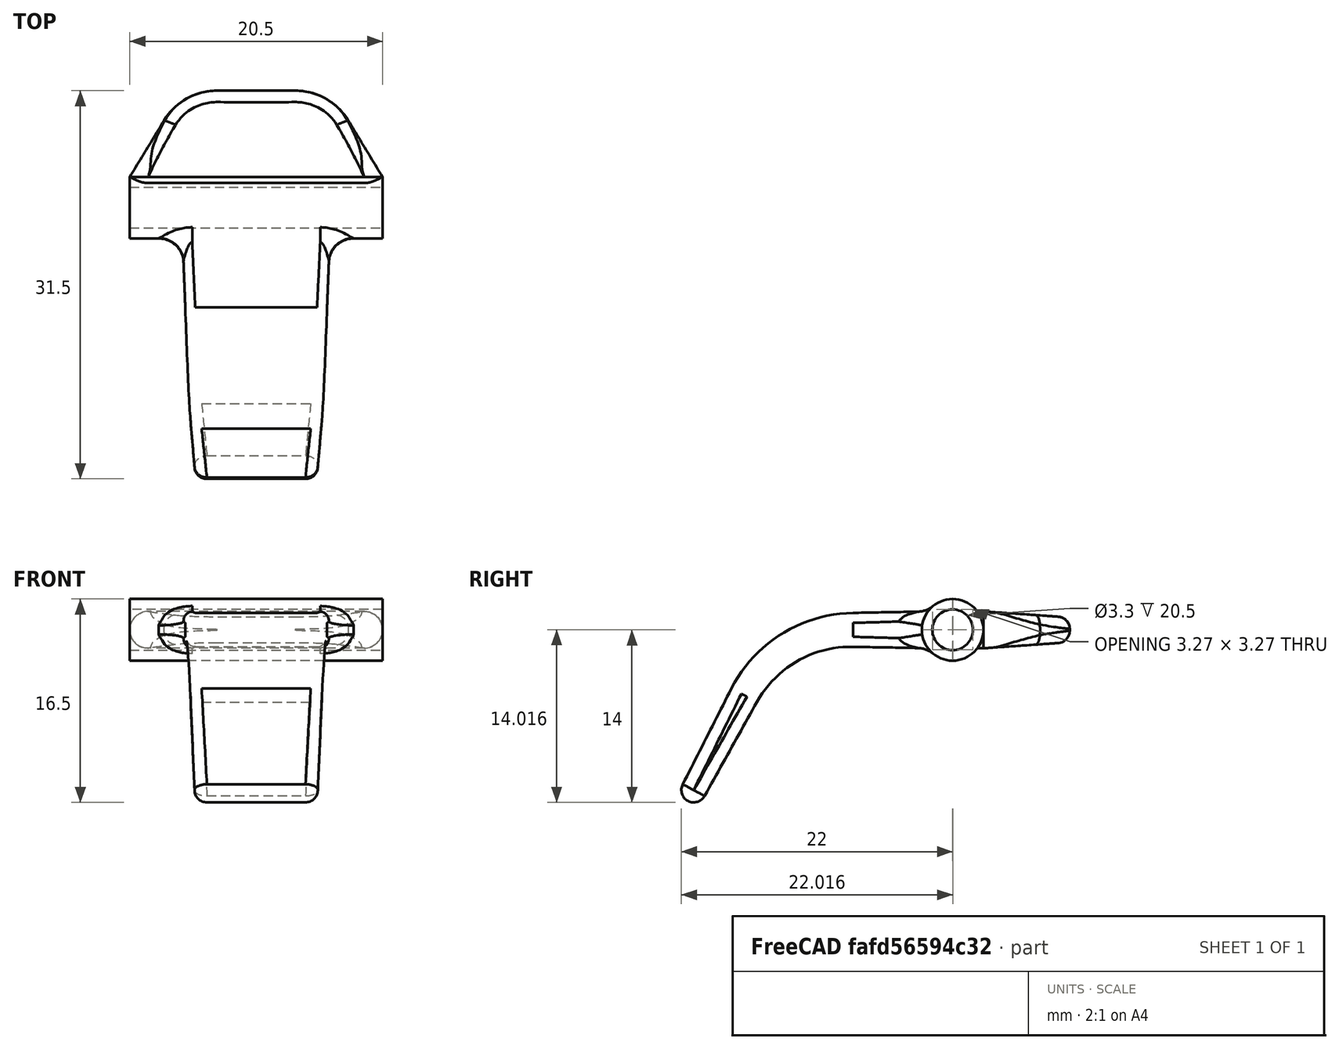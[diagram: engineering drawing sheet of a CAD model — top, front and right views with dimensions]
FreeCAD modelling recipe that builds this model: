
FCSTD DOCUMENT  (FreeCAD 0.20R28671 (Git))
Label: lengueta
License: All rights reserved
LicenseURL: http://en.wikipedia.org/wiki/All_rights_reserved
objects: TechDraw::DrawViewDimension×26, TechDraw::DrawViewAnnotation×10, Sketcher::SketchObject×8, PartDesign::Plane×5, TechDraw::DrawViewPart×5, TechDraw::DrawLeaderLine×4, PartDesign::Fillet×3, PartDesign::Pad×2, TechDraw::DrawProjGroupItem×2, TechDraw::DrawViewSection×2, PartDesign::AdditiveLoft×1, PartDesign::Pocket×1, PartDesign::AdditivePipe×1, PartDesign::Revolution×1, PartDesign::Body×1, TechDraw::DrawSVGTemplate×1, TechDraw::DrawProjGroup×1, TechDraw::DrawPage×1
note: 32 computed .brp shape members not serialized (recipe doc carries the construction recipe); baked Part::Feature solids carry a one-line shape summary decoded from their .brp

FEATURE [Sketcher::SketchObject] Sketch
  FullyConstrained = true
  MapMode = 5
  Placement = pos=(0,0,0) rot=(0.57735,0.57735,0.57735;2.0944rad)
  Support = -> [YZ_Plane]
  sketch-geometry (2):
    g0: Circle CenterX=0 CenterY=0 CenterZ=0 NormalX=0 NormalY=0 NormalZ=1 AngleXU=0 Radius=1.7
    g1: Circle CenterX=0 CenterY=0 CenterZ=0 NormalX=0 NormalY=0 NormalZ=1 AngleXU=0 Radius=2.5
  constraints (4):
    c: Coincident(g0,g-1)
    c: Diameter(g0) = 3.4
    c: Coincident(g1,g0)
    c: Diameter(g1) = 5
FEATURE [PartDesign::Pad] Pad
  Direction = (1,-2e-16,3e-16)
  Length = 20.5
  Length2 = 100
  Midplane = true
  Placement = pos=(0,0,0) rot=(0.57735,0.57735,0.57735;2.0944rad)
  Profile = -> Sketch
  ReferenceAxis = -> Sketch [N_Axis]
  Type = 0
FEATURE [PartDesign::Plane] DatumPlane
  AttachmentOffset = pos=(0,0,0) rot=(1,0,0;1.5708rad)
  Length = 60
  MapMode = 49
  Placement = pos=(10.25,2.5,3e-15) rot=(0,0.707107,0.707107;3.14159rad)
  ResizeMode = 0
  Support = -> [Pad]
  Width = 60
FEATURE [Sketcher::SketchObject] Sketch001
  ExternalGeometry = -> [Pad]
  FullyConstrained = true
  MapMode = 5
  Placement = pos=(10.25,2.5,3e-15) rot=(0,0.707107,0.707107;3.14159rad)
  Support = -> [DatumPlane]
  sketch-geometry (6):
    g0: ArcOfCircle CenterX=1.5 CenterY=0 CenterZ=0 NormalX=0 NormalY=0 NormalZ=1 AngleXU=0 Radius=1.5 StartAngle=1.5708 EndAngle=4.71239
    g1: ArcOfCircle CenterX=19 CenterY=0 CenterZ=0 NormalX=0 NormalY=0 NormalZ=1 AngleXU=0 Radius=1.5 StartAngle=4.71239 EndAngle=7.85398
    g2: LineSegment StartX=1.5 StartY=1.5 StartZ=0 EndX=19 EndY=1.5 EndZ=0
    g3: LineSegment StartX=19 StartY=-1.5 StartZ=0 EndX=1.5 EndY=-1.5 EndZ=0
    g4: LineSegment StartX=1.5 StartY=0 StartZ=0 EndX=0 EndY=0 EndZ=0
    g5: LineSegment StartX=19 StartY=0 StartZ=0 EndX=20.5 EndY=0 EndZ=0
  constraints (15):
    c: Horizontal(g3)
    c: Tangent(g3,g0) = 1.5708
    c: Tangent(g2,g0) = 1.5708
    c: Tangent(g2,g1) = 1.5708
    c: Tangent(g3,g1) = 1.5708
    c: Horizontal(g2)
    c: Coincident(g4,g0)
    c: Coincident(g4,g-1)
    c: Horizontal(g4)
    c: Coincident(g5,g1)
    c: PointOnObject(g5,g-3)
    c: Horizontal(g5)
    c: Equal(g5,g4)
    c: DistanceY(g1,g1) = 3
    c: Tangent(g1,g-3)
FEATURE [PartDesign::Pad] Pad001
  BaseFeature = -> Pad
  Direction = (4e-16,1,2e-16)
  Length = 2.5
  Length2 = 100
  Placement = pos=(0,0,0) rot=(0.57735,0.57735,0.57735;2.0944rad)
  Profile = -> Sketch001
  ReferenceAxis = -> Sketch001 [N_Axis]
  Reversed = true
  Type = 0
FEATURE [PartDesign::Plane] DatumPlane001
  AttachmentOffset = pos=(0,0,7) rot=(0,0,1;0rad)
  Length = 60
  MapMode = 5
  Placement = pos=(3.4e-15,9.5,1.2e-15) rot=(0.57735,0.57735,0.57735;4.18879rad)
  ResizeMode = 0
  Support = -> [Pad001]
  Width = 60
FEATURE [Sketcher::SketchObject] Sketch002
  FullyConstrained = true
  MapMode = 5
  Placement = pos=(3.4e-15,9.5,1.2e-15) rot=(0.57735,0.57735,0.57735;4.18879rad)
  Support = -> [DatumPlane001]
  sketch-geometry (6):
    g0: LineSegment StartX=1 StartY=6 StartZ=0 EndX=-1 EndY=6 EndZ=0
    g1: LineSegment StartX=-1 StartY=6 StartZ=0 EndX=-1 EndY=-6 EndZ=0
    g2: LineSegment StartX=-1 StartY=-6 StartZ=0 EndX=1 EndY=-6 EndZ=0
    g3: LineSegment StartX=1 StartY=-6 StartZ=0 EndX=1 EndY=6 EndZ=0
    g4: LineSegment StartX=1 StartY=6 StartZ=0 EndX=0 EndY=0 EndZ=0
    g5: LineSegment StartX=0 StartY=0 StartZ=0 EndX=-1 EndY=-6 EndZ=0
  constraints (16):
    c: Coincident(g0,g1)
    c: Coincident(g1,g2)
    c: Coincident(g2,g3)
    c: Coincident(g3,g0)
    c: Horizontal(g0)
    c: Horizontal(g2)
    c: Vertical(g1)
    c: Vertical(g3)
    c: Coincident(g4,g0)
    c: Coincident(g4,g-1)
    c: Coincident(g5,g-1)
    c: Coincident(g5,g1)
    c: Parallel(g5,g4)
    c: Equal(g4,g5)
    c: DistanceX(g1,g2) = 2
    c: DistanceY(g2,g0) = 12
FEATURE [PartDesign::AdditiveLoft] AdditiveLoft
  BaseFeature = -> Pad001
  Closed = false
  Placement = pos=(0,0,0) rot=(0.57735,0.57735,0.57735;2.0944rad)
  Profile = -> Sketch001
  Ruled = false
  Sections = -> [Sketch002]
FEATURE [PartDesign::Fillet] Fillet
  Base = -> AdditiveLoft [Edge26,Edge22]
  BaseFeature = -> AdditiveLoft
  Placement = pos=(0,0,0) rot=(0.57735,0.57735,0.57735;2.0944rad)
  Radius = 5
  SupportTransform = false
  UseAllEdges = false
FEATURE [PartDesign::Fillet] Fillet001
  Base = -> Fillet [Edge9,Edge16]
  BaseFeature = -> Fillet
  Placement = pos=(0,0,0) rot=(0.57735,0.57735,0.57735;2.0944rad)
  Radius = 1
  SupportTransform = false
  UseAllEdges = false
FEATURE [PartDesign::Plane] DatumPlane002
  AttachmentOffset = pos=(0,0,1) rot=(0,0,1;0rad)
  Length = 60
  MapMode = 11
  Placement = pos=(11.25,-4e-15,2.8e-15) rot=(0.707107,0,0.707107;3.14159rad)
  ResizeMode = 0
  Support = -> [Fillet001]
  Width = 60
FEATURE [Sketcher::SketchObject] Sketch003
  FullyConstrained = true
  MapMode = 5
  Placement = pos=(11.25,-4e-15,2.8e-15) rot=(0.707107,0,0.707107;3.14159rad)
  Support = -> [DatumPlane002]
  sketch-geometry (1):
    g0: Circle CenterX=0 CenterY=0 CenterZ=0 NormalX=0 NormalY=0 NormalZ=1 AngleXU=0 Radius=1.65
  constraints (2):
    c: Coincident(g0,g-1)
    c: Diameter(g0) = 3.3
FEATURE [PartDesign::Pocket] Pocket
  BaseFeature = -> Fillet001
  Direction = (-1,1e-16,-2e-16)
  Length = 5
  Length2 = 100
  Placement = pos=(0,0,0) rot=(0.57735,0.57735,0.57735;2.0944rad)
  Profile = -> Sketch003
  Type = 1
FEATURE [Sketcher::SketchObject] Sketch004
  FullyConstrained = true
  MapMode = 5
  Placement = pos=(0,0,0) rot=(0.57735,0.57735,0.57735;2.0944rad)
  Support = -> [YZ_Plane]
  sketch-geometry (3):
    g0: LineSegment StartX=-1.65 StartY=0 StartZ=0 EndX=-8.07917 EndY=0 EndZ=0
    g1: LineSegment StartX=-16.9086 StartY=-5.30528 StartZ=0 EndX=-21 EndY=-13 EndZ=0
    g2: ArcOfCircle CenterX=-8.07917 CenterY=-10 CenterZ=0 NormalX=0 NormalY=0 NormalZ=1 AngleXU=0 Radius=10 StartAngle=1.5708 EndAngle=2.6529
  constraints (9):
    c: Angle(g1,g0) = 2.05949
    c: Tangent(g0,g2) = -1.5708
    c: Tangent(g1,g2) = -1.5708
    c: Radius(g2) = 10
    c: Horizontal(g0)
    c: Horizontal(g0,g-1)
    c: DistanceX(g0,g-1) = 1.65
    c: DistanceX(g1,g-1) = 21
    c: DistanceY(g1,g-1) = 13
FEATURE [PartDesign::Plane] DatumPlane003
  Length = 60
  MapMode = 7
  Placement = pos=(-4e-16,-1.65,4e-16) rot=(0,0.707107,0.707107;3.14159rad)
  ResizeMode = 0
  Support = -> [Sketch004]
  Width = 60
FEATURE [Sketcher::SketchObject] Sketch005
  FullyConstrained = true
  MapMode = 5
  Placement = pos=(-4e-16,-1.65,4e-16) rot=(0,0.707107,0.707107;3.14159rad)
  Support = -> [DatumPlane003]
  sketch-geometry (10):
    g0: LineSegment StartX=-5.25 StartY=1.5 StartZ=0 EndX=5.25 EndY=1.5 EndZ=0
    g1: LineSegment StartX=6 StartY=0.75 StartZ=0 EndX=6 EndY=-0.75 EndZ=0
    g2: LineSegment StartX=5.25 StartY=-1.5 StartZ=0 EndX=-5.25 EndY=-1.5 EndZ=0
    g3: LineSegment StartX=-6 StartY=-0.75 StartZ=0 EndX=-6 EndY=0.75 EndZ=0
    g4: ArcOfCircle CenterX=-5.25 CenterY=0.75 CenterZ=0 NormalX=0 NormalY=0 NormalZ=1 AngleXU=0 Radius=0.75 StartAngle=1.5708 EndAngle=3.14159
    g5: ArcOfCircle CenterX=5.25 CenterY=0.75 CenterZ=0 NormalX=0 NormalY=0 NormalZ=1 AngleXU=0 Radius=0.75 StartAngle=1.3e-15 EndAngle=1.5708
    g6: ArcOfCircle CenterX=5.25 CenterY=-0.75 CenterZ=0 NormalX=0 NormalY=0 NormalZ=1 AngleXU=0 Radius=0.75 StartAngle=4.71239 EndAngle=6.28319
    g7: ArcOfCircle CenterX=-5.25 CenterY=-0.75 CenterZ=0 NormalX=0 NormalY=0 NormalZ=1 AngleXU=0 Radius=0.75 StartAngle=3.14159 EndAngle=4.71239
    g8: LineSegment StartX=-5.25 StartY=0.75 StartZ=0 EndX=0 EndY=-1e-16 EndZ=0
    g9: LineSegment StartX=0 StartY=0 StartZ=0 EndX=5.25 EndY=-0.75 EndZ=0
  constraints (24):
    c: Horizontal(g0)
    c: Horizontal(g2)
    c: Vertical(g1)
    c: Vertical(g3)
    c: Tangent(g0,g4) = 1.5708
    c: Tangent(g3,g4) = 1.5708
    c: Tangent(g0,g5) = 1.5708
    c: Tangent(g1,g5) = 1.5708
    c: Tangent(g1,g6) = 1.5708
    c: Tangent(g2,g6) = 1.5708
    c: Tangent(g2,g7) = 1.5708
    c: Tangent(g3,g7) = 1.5708
    c: Equal(g7,g4)
    c: Equal(g4,g5)
    c: Equal(g5,g6)
    c: DistanceY(g2,g0) = 3
    c: DistanceX(g3,g1) = 12
    c: Radius(g6) = 0.75
    c: Coincident(g8,g4)
    c: Coincident(g8,g-1)
    c: Coincident(g9,g-1)
    c: Coincident(g9,g6)
    c: Parallel(g9,g8)
    c: Equal(g9,g8)
FEATURE [PartDesign::Plane] DatumPlane004
  Length = 61.6294
  MapMode = 7
  Placement = pos=(-1.8e-15,-21,-13) rot=(0,0.241922,0.970296;3.14159rad)
  ResizeMode = 0
  Support = -> [Sketch004]
  Width = 79.2503
FEATURE [Sketcher::SketchObject] Sketch006
  FullyConstrained = true
  MapMode = 5
  Placement = pos=(-1.8e-15,-21,-13) rot=(0,0.241922,0.970296;3.14159rad)
  Support = -> [DatumPlane004]
  sketch-geometry (10):
    g0: LineSegment StartX=-4 StartY=1 StartZ=0 EndX=4 EndY=1 EndZ=0
    g1: LineSegment StartX=5 StartY=4.5072e-12 StartZ=0 EndX=5 EndY=-4.5073e-12 EndZ=0
    g2: LineSegment StartX=4 StartY=-1 StartZ=0 EndX=-4 EndY=-1 EndZ=0
    g3: LineSegment StartX=-5 StartY=-4.5072e-12 StartZ=0 EndX=-5 EndY=4.5072e-12 EndZ=0
    g4: ArcOfCircle CenterX=-4 CenterY=2.1472e-12 CenterZ=0 NormalX=0 NormalY=0 NormalZ=1 AngleXU=0 Radius=1 StartAngle=1.5708 EndAngle=3.14159
    g5: ArcOfCircle CenterX=4 CenterY=2.1472e-12 CenterZ=0 NormalX=0 NormalY=0 NormalZ=1 AngleXU=0 Radius=1 StartAngle=2.36e-12 EndAngle=1.5708
    g6: ArcOfCircle CenterX=-4 CenterY=-2.1474e-12 CenterZ=0 NormalX=0 NormalY=0 NormalZ=1 AngleXU=0 Radius=1 StartAngle=3.14159 EndAngle=4.71239
    g7: ArcOfCircle CenterX=4 CenterY=-2.1472e-12 CenterZ=0 NormalX=0 NormalY=0 NormalZ=1 AngleXU=0 Radius=1 StartAngle=4.71239 EndAngle=6.28319
    g8: LineSegment StartX=-4 StartY=2.1472e-12 StartZ=0 EndX=0 EndY=0 EndZ=0
    g9: LineSegment StartX=0 StartY=0 StartZ=0 EndX=4 EndY=-2.1472e-12 EndZ=0
  constraints (24):
    c: Horizontal(g0)
    c: Horizontal(g2)
    c: Vertical(g1)
    c: Vertical(g3)
    c: Tangent(g0,g4) = 1.5708
    c: Tangent(g3,g4) = 1.5708
    c: Tangent(g0,g5) = 1.5708
    c: Tangent(g1,g5) = 1.5708
    c: Tangent(g3,g6) = 1.5708
    c: Tangent(g2,g6) = 1.5708
    c: Tangent(g1,g7) = 1.5708
    c: Tangent(g2,g7) = 1.5708
    c: Equal(g4,g6)
    c: Equal(g6,g5)
    c: Equal(g5,g7)
    c: Coincident(g8,g4)
    c: Coincident(g9,g8)
    c: Coincident(g9,g7)
    c: Coincident(g8,g-1)
    c: Equal(g9,g8)
    c: Parallel(g9,g8)
    c: Radius(g4) = 1
    c: DistanceY(g2,g0) = 2
    c: DistanceX(g3,g1) = 10
FEATURE [PartDesign::AdditivePipe] AdditivePipe
  AuxilleryCurvelinear = true
  AuxillerySpineTangent = false
  BaseFeature = -> Pocket
  Binormal = (0,0,0)
  Mode = 0
  Placement = pos=(0,0,0) rot=(0.57735,0.57735,0.57735;2.0944rad)
  Profile = -> Sketch005
  Sections = -> [Sketch006]
  Spine = -> Sketch004
  SpineTangent = false
  Transformation = 1
  Transition = 0
FEATURE [Sketcher::SketchObject] Sketch007
  ExternalGeometry = -> [AdditivePipe]
  FullyConstrained = true
  MapMode = 5
  Placement = pos=(0,-10.0172,-18.8396) rot=(0.696367,0.696367,-0.173624;2.79777rad)
  Support = -> [AdditivePipe]
  sketch-geometry (5):
    g0: LineSegment StartX=-12.4388 StartY=5 StartZ=0 EndX=-12.4388 EndY=-5 EndZ=0
    g1: LineSegment StartX=-12.4388 StartY=5 StartZ=0 EndX=-12.4388 EndY=-5 EndZ=0
    g2: LineSegment StartX=-13.4388 StartY=-4 StartZ=0 EndX=-13.4388 EndY=4 EndZ=0
    g3: ArcOfCircle CenterX=-12.4388 CenterY=4 CenterZ=0 NormalX=0 NormalY=0 NormalZ=1 AngleXU=0 Radius=1 StartAngle=1.5708 EndAngle=3.14159
    g4: ArcOfCircle CenterX=-12.4388 CenterY=-4 CenterZ=0 NormalX=0 NormalY=0 NormalZ=1 AngleXU=0 Radius=1 StartAngle=3.14159 EndAngle=4.71239
  constraints (10):
    c: Coincident(g0,g-5)
    c: Coincident(g0,g-3)
    c: Coincident(g1,g0)
    c: Coincident(g1,g0)
    c: Coincident(g2,g-4)
    c: Coincident(g2,g-5)
    c: Coincident(g3,g1)
    c: Coincident(g4,g1)
    c: Tangent(g4,g2) = 1.5708
    c: Tangent(g3,g2) = 1.5708
FEATURE [PartDesign::Revolution] Revolution
  Angle = 360
  Axis = (-10,7.9564e-12,-4.2306e-12)
  Base = (5,-21,-13)
  BaseFeature = -> AdditivePipe
  Placement = pos=(0,0,0) rot=(0.57735,0.57735,0.57735;2.0944rad)
  Profile = -> Sketch007
  ReferenceAxis = -> Sketch007 [Axis0]
  Reversed = true
FEATURE [PartDesign::Fillet] Fillet002
  Base = -> Revolution [Edge42]
  BaseFeature = -> Revolution
  Placement = pos=(0,0,0) rot=(0.57735,0.57735,0.57735;2.0944rad)
  Radius = 2
  SupportTransform = false
  UseAllEdges = false
FEATURE [PartDesign::Body] Body
  Group = -> [Sketch,Pad,DatumPlane,Sketch001,Pad001,DatumPlane001,Sketch002,AdditiveLoft,Fillet,Fillet001,DatumPlane002,Sketch003,Pocket,Sketch004,DatumPlane003,Sketch005,DatumPlane004,Sketch006,AdditivePipe,Sketch007,Revolution,Fillet002]
  Origin = -> Origin
  Tip = -> Fillet002
FEATURE [TechDraw::DrawSVGTemplate] Template
  EditableTexts = AUTHOR_NAME=Daniel García García; DATE=14-04-2022; DN=11; DOCUMENT_TYPE=Plano de Pieza; PN=14; REVISION=1; SCALE=2:1; SHEET=11/15; SIZE=A4; TITLELINE-1=Lengüeta
  Height = 210
  Orientation = 1
  Width = 297
FEATURE [TechDraw::DrawProjGroupItem] ProjItem  label="Front"
  CoarseView = false
  Direction = (-1,0,0)
  Focus = 100
  HardHidden = true
  IsoCount = 0
  IsoHidden = false
  IsoVisible = false
  LockPosition = true
  Perspective = false
  Rotation = 0
  RotationVector = (0,-1,0)
  Scale = 2
  ScaleType = 2
  SeamHidden = false
  SeamVisible = true
  SmoothHidden = false
  SmoothVisible = true
  Source = -> [Fillet002]
  Type = 0
  X = 0
  XDirection = (0,-1,0)
  Y = 0
FEATURE [TechDraw::DrawProjGroupItem] ProjItem001  label="Top"
  CoarseView = false
  Direction = (0,0,1)
  Focus = 100
  HardHidden = false
  IsoCount = 0
  IsoHidden = false
  IsoVisible = false
  LockPosition = true
  Perspective = false
  Rotation = 0
  RotationVector = (1,0,0)
  ScaleType = 2
  SeamHidden = false
  SeamVisible = true
  SmoothHidden = false
  SmoothVisible = true
  Source = -> [Fillet002]
  Type = 4
  X = 0
  XDirection = (0,-1,0)
  Y = -60.9884
FEATURE [TechDraw::DrawProjGroup] ProjGroup
  Anchor = -> ProjItem
  AutoDistribute = true
  LockPosition = false
  ProjectionType = 0
  Rotation = 0
  Scale = 2
  ScaleType = 2
  Source = -> [Fillet002]
  Views = -> [ProjItem,ProjItem001]
  X = 212.008
  Y = 158.001
  spacingX = 15
  spacingY = 15
FEATURE [TechDraw::DrawViewDimension] Dimension
  AngleOverride = false
  Arbitrary = false
  ArbitraryTolerances = false
  EqualTolerance = true
  ExtensionAngle = 0
  FormatSpec = ⌀%.2w
  FormatSpecOverTolerance = %+.2w
  FormatSpecUnderTolerance = %+.2w
  Inverted = false
  LineAngle = 0
  LockPosition = false
  MeasureType = 1
  OverTolerance = 0
  References2D = -> [ProjItem]
  Rotation = 0
  ScaleType = 0
  TheoreticalExact = false
  Type = 5
  UnderTolerance = 0
  X = -30.3666
  Y = 3.71542
FEATURE [TechDraw::DrawViewDimension] Dimension001
  AngleOverride = false
  Arbitrary = false
  ArbitraryTolerances = false
  EqualTolerance = true
  ExtensionAngle = 0
  FormatSpec = ⌀%.2w
  FormatSpecOverTolerance = %+.2w
  FormatSpecUnderTolerance = %+.2w
  Inverted = false
  LineAngle = 0
  LockPosition = false
  MeasureType = 1
  OverTolerance = 0
  References2D = -> [ProjItem]
  Rotation = 0
  ScaleType = 0
  TheoreticalExact = false
  Type = 5
  UnderTolerance = 0
  X = -26.8824
  Y = 29.5051
FEATURE [TechDraw::DrawViewPart] View
  CoarseView = false
  Direction = (-1,0,0)
  Focus = 100
  HardHidden = false
  IsoCount = 0
  IsoHidden = false
  IsoVisible = false
  LockPosition = false
  Perspective = false
  Rotation = 0
  Scale = 2
  ScaleType = 2
  SeamHidden = false
  SeamVisible = true
  SmoothHidden = false
  SmoothVisible = true
  Source = -> [Sketch004]
  X = 222.198
  XDirection = (0,-1,0)
  Y = 156.544
FEATURE [TechDraw::DrawViewDimension] Dimension003
  AngleOverride = false
  Arbitrary = false
  ArbitraryTolerances = false
  EqualTolerance = true
  ExtensionAngle = 0
  FormatSpec = %.2w
  FormatSpecOverTolerance = %+.2w
  FormatSpecUnderTolerance = %+.2w
  Inverted = false
  LineAngle = 0
  LockPosition = false
  MeasureType = 1
  OverTolerance = 0
  References2D = -> [View]
  Rotation = 0
  ScaleType = 0
  TheoreticalExact = false
  Type = 1
  UnderTolerance = 0
  X = -12.6215
  Y = 2.03085
FEATURE [TechDraw::DrawViewDimension] Dimension004
  AngleOverride = false
  Arbitrary = false
  ArbitraryTolerances = false
  EqualTolerance = true
  ExtensionAngle = 0
  FormatSpec = R%.2w
  FormatSpecOverTolerance = %+.2w
  FormatSpecUnderTolerance = %+.2w
  Inverted = false
  LineAngle = 0
  LockPosition = false
  MeasureType = 1
  OverTolerance = 0
  References2D = -> [View]
  Rotation = 0
  ScaleType = 0
  TheoreticalExact = false
  Type = 4
  UnderTolerance = 0
  X = 19.0508
  Y = 20.7748
FEATURE [TechDraw::DrawViewDimension] Dimension005
  AngleOverride = false
  Arbitrary = false
  ArbitraryTolerances = false
  EqualTolerance = true
  ExtensionAngle = 0
  FormatSpec = %.2w
  FormatSpecOverTolerance = %+.2w
  FormatSpecUnderTolerance = %+.2w
  Inverted = false
  LineAngle = 0
  LockPosition = false
  MeasureType = 1
  OverTolerance = 0
  References2D = -> [View]
  Rotation = 0
  ScaleType = 0
  TheoreticalExact = false
  Type = 1
  UnderTolerance = 0
  X = -2.12128
  Y = -10.6356
FEATURE [TechDraw::DrawViewDimension] Dimension006
  AngleOverride = false
  Arbitrary = false
  ArbitraryTolerances = false
  EqualTolerance = true
  ExtensionAngle = 0
  FormatSpec = %.2w
  FormatSpecOverTolerance = %+.2w
  FormatSpecUnderTolerance = %+.2w
  Inverted = false
  LineAngle = 0
  LockPosition = false
  MeasureType = 1
  OverTolerance = 0
  References2D = -> [View]
  Rotation = 0
  ScaleType = 0
  TheoreticalExact = false
  Type = 2
  UnderTolerance = 0
  X = -53.3039
  Y = 2.09206
FEATURE [TechDraw::DrawViewDimension] Dimension007
  AngleOverride = false
  Arbitrary = false
  ArbitraryTolerances = false
  EqualTolerance = true
  ExtensionAngle = 0
  FormatSpec = %.2w
  FormatSpecOverTolerance = %+.2w
  FormatSpecUnderTolerance = %+.2w
  Inverted = false
  LineAngle = 0
  LockPosition = false
  MeasureType = 1
  OverTolerance = 0
  References2D = -> [View]
  Rotation = 0
  ScaleType = 0
  TheoreticalExact = false
  Type = 6
  UnderTolerance = 0
  X = 0.679897
  Y = 4.89526
FEATURE [TechDraw::DrawViewSection] SectionView  label="Section A - A"
  BaseView = -> ProjItem001
  CoarseView = false
  CutSurfaceDisplay = 2
  Direction = (0,-1,0)
  FileGeomPattern = <path>
  FileHatchPattern = <path>
  Focus = 100
  FuseBeforeCut = false
  HardHidden = false
  HatchScale = 1
  IsoCount = 0
  IsoHidden = false
  IsoVisible = false
  LockPosition = false
  NameGeomPattern = Diamond
  Perspective = false
  Rotation = 0
  Scale = 2
  ScaleType = 2
  SeamHidden = false
  SeamVisible = true
  SectionDirection = 1
  SectionNormal = (0,-1,0)
  SectionOrigin = (0,2.5,-5.76)
  SectionSymbol = A
  SmoothHidden = false
  SmoothVisible = true
  Source = -> [Sketch001,Sketch002]
  X = 114.023
  XDirection = (0,0,-1)
  Y = 93.9563
FEATURE [TechDraw::DrawViewDimension] Dimension009
  AngleOverride = false
  Arbitrary = false
  ArbitraryTolerances = false
  EqualTolerance = true
  ExtensionAngle = 0
  FormatSpec = %.2w
  FormatSpecOverTolerance = %+.2w
  FormatSpecUnderTolerance = %+.2w
  Inverted = false
  LineAngle = 0
  LockPosition = false
  MeasureType = 1
  OverTolerance = 0
  References2D = -> [SectionView]
  Rotation = 0
  ScaleType = 0
  TheoreticalExact = false
  Type = 2
  UnderTolerance = 0
  X = 17.8579
  Y = 3.43989
FEATURE [TechDraw::DrawViewDimension] Dimension010
  AngleOverride = false
  Arbitrary = false
  ArbitraryTolerances = false
  EqualTolerance = true
  ExtensionAngle = 0
  FormatSpec = %.2w
  FormatSpecOverTolerance = %+.2w
  FormatSpecUnderTolerance = %+.2w
  Inverted = false
  LineAngle = 0
  LockPosition = false
  MeasureType = 1
  OverTolerance = 0
  References2D = -> [SectionView]
  Rotation = 0
  ScaleType = 0
  TheoreticalExact = false
  Type = 1
  UnderTolerance = 0
  X = 11.5137
  Y = 28.929
FEATURE [TechDraw::DrawViewDimension] Dimension011
  AngleOverride = false
  Arbitrary = false
  ArbitraryTolerances = false
  EqualTolerance = true
  ExtensionAngle = 0
  FormatSpec = R%.2w
  FormatSpecOverTolerance = %+.2w
  FormatSpecUnderTolerance = %+.2w
  Inverted = false
  LineAngle = 0
  LockPosition = false
  MeasureType = 1
  OverTolerance = 0
  References2D = -> [SectionView]
  Rotation = 0
  ScaleType = 0
  TheoreticalExact = false
  Type = 4
  UnderTolerance = 0
  X = -20.6562
  Y = 31.6647
FEATURE [TechDraw::DrawViewDimension] Dimension012
  AngleOverride = false
  Arbitrary = true
  ArbitraryTolerances = false
  EqualTolerance = true
  ExtensionAngle = 0
  FormatSpec = R5
  FormatSpecOverTolerance = %+.2w
  FormatSpecUnderTolerance = %+.2w
  Inverted = false
  LineAngle = 0
  LockPosition = false
  MeasureType = 1
  OverTolerance = 0
  References2D = -> [ProjItem001]
  Rotation = 0
  ScaleType = 0
  TheoreticalExact = false
  Type = 4
  UnderTolerance = 0
  X = -42.3041
  Y = 28.5999
FEATURE [TechDraw::DrawViewDimension] Dimension013
  AngleOverride = false
  Arbitrary = false
  ArbitraryTolerances = false
  EqualTolerance = true
  ExtensionAngle = 0
  FormatSpec = R%.2w
  FormatSpecOverTolerance = %+.2w
  FormatSpecUnderTolerance = %+.2w
  Inverted = false
  LineAngle = 0
  LockPosition = false
  MeasureType = 0
  OverTolerance = 0
  References2D = -> [ProjItem,Fillet]
  References3D = -> [Fillet]
  Rotation = 0
  ScaleType = 0
  TheoreticalExact = false
  Type = 4
  UnderTolerance = 0
  X = -40.3406
  Y = 23.7964
FEATURE [TechDraw::DrawViewDimension] Dimension014
  AngleOverride = false
  Arbitrary = true
  ArbitraryTolerances = false
  EqualTolerance = true
  ExtensionAngle = 0
  FormatSpec = R1
  FormatSpecOverTolerance = %+.2w
  FormatSpecUnderTolerance = %+.2w
  Inverted = false
  LineAngle = 0
  LockPosition = false
  MeasureType = 1
  OverTolerance = 0
  References2D = -> [ProjItem]
  Rotation = 0
  ScaleType = 0
  TheoreticalExact = false
  Type = 4
  UnderTolerance = 0
  X = -39.7221
  Y = 26.378
FEATURE [TechDraw::DrawViewSection] SectionView001  label="Section B - B"
  BaseView = -> ProjItem001
  CoarseView = false
  CutSurfaceDisplay = 2
  Direction = (0,-1,0)
  FileGeomPattern = <path>
  FileHatchPattern = <path>
  Focus = 100
  FuseBeforeCut = false
  HardHidden = false
  HatchScale = 1
  IsoCount = 0
  IsoHidden = false
  IsoVisible = false
  LockPosition = false
  NameGeomPattern = Diamond
  Perspective = false
  Rotation = 0
  Scale = 2
  ScaleType = 2
  SeamHidden = false
  SeamVisible = true
  SectionDirection = 1
  SectionNormal = (0,-1,0)
  SectionOrigin = (0,9.4,-5.76)
  SectionSymbol = B
  SmoothHidden = false
  SmoothVisible = true
  Source = -> [Fillet002,Sketch002]
  X = 70.5325
  XDirection = (0,0,-1)
  Y = 95.4195
FEATURE [TechDraw::DrawViewPart] View001
  CoarseView = false
  Direction = (0,1,0)
  Focus = 100
  HardHidden = false
  IsoCount = 0
  IsoHidden = false
  IsoVisible = false
  LockPosition = true
  Perspective = false
  Rotation = 0
  Scale = 2
  ScaleType = 2
  SeamHidden = false
  SeamVisible = true
  SmoothHidden = false
  SmoothVisible = true
  Source = -> [Sketch001]
  X = 110
  XDirection = (0,0,-1)
  Y = 96.9447
FEATURE [TechDraw::DrawViewPart] View002
  CoarseView = false
  Direction = (0,1,0)
  Focus = 100
  HardHidden = false
  IsoCount = 0
  IsoHidden = false
  IsoVisible = false
  LockPosition = true
  Perspective = false
  Rotation = 0
  Scale = 2
  ScaleType = 2
  SeamHidden = false
  SeamVisible = true
  SmoothHidden = false
  SmoothVisible = true
  Source = -> [Sketch002]
  X = 60
  XDirection = (0,0,-1)
  Y = 96.64
FEATURE [TechDraw::DrawViewDimension] Dimension015
  AngleOverride = false
  Arbitrary = false
  ArbitraryTolerances = false
  EqualTolerance = true
  ExtensionAngle = 0
  FormatSpec = %.2w
  FormatSpecOverTolerance = %+.2w
  FormatSpecUnderTolerance = %+.2w
  Inverted = false
  LineAngle = 0
  LockPosition = false
  MeasureType = 1
  OverTolerance = 0
  References2D = -> [View002]
  Rotation = 0
  ScaleType = 0
  TheoreticalExact = false
  Type = 2
  UnderTolerance = 0
  X = -9.70269
  Y = 3.31588
FEATURE [TechDraw::DrawViewDimension] Dimension016
  AngleOverride = false
  Arbitrary = false
  ArbitraryTolerances = false
  EqualTolerance = true
  ExtensionAngle = 0
  FormatSpec = %.2w
  FormatSpecOverTolerance = %+.2w
  FormatSpecUnderTolerance = %+.2w
  Inverted = false
  LineAngle = 0
  LockPosition = false
  MeasureType = 1
  OverTolerance = 0
  References2D = -> [View002]
  Rotation = 0
  ScaleType = 0
  TheoreticalExact = false
  Type = 1
  UnderTolerance = 0
  X = -0.407938
  Y = 15.299
FEATURE [TechDraw::DrawViewDimension] Dimension017
  AngleOverride = false
  Arbitrary = false
  ArbitraryTolerances = false
  EqualTolerance = true
  ExtensionAngle = 0
  FormatSpec = %.2w
  FormatSpecOverTolerance = %+.2w
  FormatSpecUnderTolerance = %+.2w
  Inverted = false
  LineAngle = 0
  LockPosition = false
  MeasureType = 1
  OverTolerance = 0
  References2D = -> [View001]
  Rotation = 0
  ScaleType = 0
  TheoreticalExact = false
  Type = 1
  UnderTolerance = 0
  X = -14.5649
  Y = 31.22
FEATURE [TechDraw::DrawViewDimension] Dimension018
  AngleOverride = false
  Arbitrary = false
  ArbitraryTolerances = false
  EqualTolerance = true
  ExtensionAngle = 0
  FormatSpec = %.2w
  FormatSpecOverTolerance = %+.2w
  FormatSpecUnderTolerance = %+.2w
  Inverted = false
  LineAngle = 0
  LockPosition = false
  MeasureType = 1
  OverTolerance = 0
  References2D = -> [ProjItem001]
  Rotation = 0
  ScaleType = 0
  TheoreticalExact = false
  Type = 2
  UnderTolerance = 0
  X = -42.7922
  Y = 2.5
FEATURE [TechDraw::DrawViewDimension] Dimension019
  AngleOverride = false
  Arbitrary = false
  ArbitraryTolerances = false
  EqualTolerance = true
  ExtensionAngle = 0
  FormatSpec = %.2w
  FormatSpecOverTolerance = %+.2w
  FormatSpecUnderTolerance = %+.2w
  Inverted = false
  LineAngle = 0
  LockPosition = false
  MeasureType = 1
  OverTolerance = 0
  References2D = -> [View001]
  Rotation = 0
  ScaleType = 0
  TheoreticalExact = false
  Type = 2
  UnderTolerance = 0
  X = 7.17971
  Y = 3.47905
FEATURE [TechDraw::DrawViewDimension] Dimension020
  AngleOverride = false
  Arbitrary = false
  ArbitraryTolerances = false
  EqualTolerance = true
  ExtensionAngle = 0
  FormatSpec = R%.2w
  FormatSpecOverTolerance = %+.2w
  FormatSpecUnderTolerance = %+.2w
  Inverted = false
  LineAngle = 0
  LockPosition = false
  MeasureType = 1
  OverTolerance = 0
  References2D = -> [View001]
  Rotation = 0
  ScaleType = 0
  TheoreticalExact = false
  Type = 4
  UnderTolerance = 0
  X = -12.6949
  Y = -20.199
FEATURE [TechDraw::DrawViewAnnotation] Annotation
  Font = osifont
  LineSpace = 80
  LockPosition = true
  MaxWidth = -1
  Rotation = 0
  ScaleType = 0
  Text = Sección B - B'
  TextSize = 5
  TextStyle = 0
  X = 63.2493
  Y = 75.7182
FEATURE [TechDraw::DrawViewAnnotation] Annotation001
  Font = osifont
  LineSpace = 80
  LockPosition = true
  MaxWidth = -1
  Rotation = 0
  ScaleType = 0
  Text = Sección A - A'
  TextSize = 5
  TextStyle = 0
  X = 112.442
  Y = 62.4633
FEATURE [TechDraw::DrawViewAnnotation] Annotation002
  Font = osifont
  LineSpace = 80
  LockPosition = false
  MaxWidth = -1
  Rotation = 0
  ScaleType = 0
  Text = '
  TextSize = 5
  TextStyle = 0
  X = 196.685
  Y = 52.367
FEATURE [TechDraw::DrawViewAnnotation] Annotation003
  Font = osifont
  LineSpace = 80
  LockPosition = false
  MaxWidth = -1
  Rotation = 0
  ScaleType = 0
  Text = '
  TextSize = 5
  TextStyle = 0
  X = 183.712
  Y = 52.367
FEATURE [TechDraw::DrawViewDimension] Dimension021
  AngleOverride = false
  Arbitrary = false
  ArbitraryTolerances = false
  EqualTolerance = true
  ExtensionAngle = 0
  FormatSpec = R%.2w
  FormatSpecOverTolerance = %+.2w
  FormatSpecUnderTolerance = %+.2w
  Inverted = false
  LineAngle = 0
  LockPosition = false
  MeasureType = 1
  OverTolerance = 0
  References2D = -> [ProjItem]
  Rotation = 0
  ScaleType = 0
  TheoreticalExact = false
  Type = 4
  UnderTolerance = 0
  X = 38.084
  Y = -19.3956
FEATURE [TechDraw::DrawLeaderLine] LeaderLine
  AutoHorizontal = false
  EndSymbol = 7
  LeaderParent = -> ProjItem
  LockPosition = true
  Rotation = 0
  Scalable = false
  ScaleType = 0
  StartSymbol = 0
  WayPoints = (2) [(0,0,0),(74.9763,141.427,0)]
  X = 11.1786
  Y = -9.14235
FEATURE [TechDraw::DrawLeaderLine] LeaderLine001
  AutoHorizontal = false
  EndSymbol = 7
  LeaderParent = -> ProjItem001
  LockPosition = true
  Rotation = 0
  Scalable = false
  ScaleType = 0
  StartSymbol = 0
  WayPoints = (2) [(0,0,0),(80.2279,149.577,0)]
  X = 18.2796
  Y = 27.6505
FEATURE [TechDraw::DrawViewAnnotation] Annotation004
  Font = osifont
  LineSpace = 80
  LockPosition = true
  MaxWidth = -1
  Rotation = 0
  ScaleType = 0
  Text = C
  TextSize = 5
  TextStyle = 0
  X = 242.226
  Y = 120.903
FEATURE [TechDraw::DrawViewAnnotation] Annotation005
  Font = osifont
  LineSpace = 80
  LockPosition = true
  MaxWidth = -1
  Rotation = 0
  ScaleType = 0
  Text = C'
  TextSize = 5
  TextStyle = 0
  X = 258.467
  Y = 128.009
FEATURE [TechDraw::DrawLeaderLine] LeaderLine002
  AutoHorizontal = true
  EndSymbol = 7
  LeaderParent = -> ProjItem
  LockPosition = true
  Rotation = 0
  Scalable = false
  ScaleType = 0
  StartSymbol = 0
  WayPoints = (2) [(0,0,0),(169.85,0,0)]
  X = -4.66003
  Y = 11.627
FEATURE [TechDraw::DrawLeaderLine] LeaderLine003
  AutoHorizontal = true
  EndSymbol = 7
  LeaderParent = -> ProjItem
  LockPosition = true
  Rotation = 0
  Scalable = false
  ScaleType = 0
  StartSymbol = 0
  WayPoints = (2) [(0,0,0),(173.838,0,0)]
  X = -4.57066
  Y = -0.34925
FEATURE [TechDraw::DrawViewAnnotation] Annotation006
  Font = osifont
  LineSpace = 80
  LockPosition = false
  MaxWidth = -1
  Rotation = 0
  ScaleType = 0
  Text = D
  TextSize = 5
  TextStyle = 0
  X = 222.006
  Y = 179.561
FEATURE [TechDraw::DrawViewAnnotation] Annotation007
  Font = osifont
  LineSpace = 80
  LockPosition = true
  MaxWidth = -1
  Rotation = 0
  ScaleType = 0
  Text = D'
  TextSize = 5
  TextStyle = 0
  X = 222.877
  Y = 155.75
FEATURE [TechDraw::DrawViewPart] View003
  CoarseView = false
  Direction = (0,1,0)
  Focus = 100
  HardHidden = false
  IsoCount = 0
  IsoHidden = false
  IsoVisible = false
  LockPosition = true
  Perspective = false
  Rotation = 0
  Scale = 2
  ScaleType = 2
  SeamHidden = false
  SeamVisible = true
  SmoothHidden = false
  SmoothVisible = true
  Source = -> [Sketch005]
  X = 63.3432
  XDirection = (0,0,-1)
  Y = 162.585
FEATURE [TechDraw::DrawViewPart] View004
  CoarseView = false
  Direction = (0,0.469,0.883)
  Focus = 100
  HardHidden = false
  IsoCount = 0
  IsoHidden = false
  IsoVisible = false
  LockPosition = true
  Perspective = false
  Rotation = 0
  Scale = 2
  ScaleType = 2
  SeamHidden = false
  SeamVisible = true
  SmoothHidden = false
  SmoothVisible = true
  Source = -> [Sketch006]
  X = 112.488
  XDirection = (0,0.883,-0.469)
  Y = 163.689
FEATURE [TechDraw::DrawViewDimension] Dimension022
  AngleOverride = false
  Arbitrary = false
  ArbitraryTolerances = false
  EqualTolerance = true
  ExtensionAngle = 0
  FormatSpec = %.2w
  FormatSpecOverTolerance = %+.2w
  FormatSpecUnderTolerance = %+.2w
  Inverted = false
  LineAngle = 0
  LockPosition = false
  MeasureType = 1
  OverTolerance = 0
  References2D = -> [View003]
  Rotation = 0
  ScaleType = 0
  TheoreticalExact = false
  Type = 2
  UnderTolerance = 0
  X = -14.826
  Y = 2.90794
FEATURE [TechDraw::DrawViewDimension] Dimension023
  AngleOverride = false
  Arbitrary = false
  ArbitraryTolerances = false
  EqualTolerance = true
  ExtensionAngle = 0
  FormatSpec = %.2w
  FormatSpecOverTolerance = %+.2w
  FormatSpecUnderTolerance = %+.2w
  Inverted = false
  LineAngle = 0
  LockPosition = false
  MeasureType = 1
  OverTolerance = 0
  References2D = -> [View003]
  Rotation = 0
  ScaleType = 0
  TheoreticalExact = false
  Type = 1
  UnderTolerance = 0
  X = -9.59471
  Y = 21.8115
FEATURE [TechDraw::DrawViewDimension] Dimension024
  AngleOverride = false
  Arbitrary = false
  ArbitraryTolerances = false
  EqualTolerance = true
  ExtensionAngle = 0
  FormatSpec = R%.2w
  FormatSpecOverTolerance = %+.2w
  FormatSpecUnderTolerance = %+.2w
  Inverted = false
  LineAngle = 0
  LockPosition = false
  MeasureType = 1
  OverTolerance = 0
  References2D = -> [View003]
  Rotation = 0
  ScaleType = 0
  TheoreticalExact = false
  Type = 4
  UnderTolerance = 0
  X = 18.5336
  Y = 19.7404
FEATURE [TechDraw::DrawViewDimension] Dimension025
  AngleOverride = false
  Arbitrary = false
  ArbitraryTolerances = false
  EqualTolerance = true
  ExtensionAngle = 0
  FormatSpec = %.2w
  FormatSpecOverTolerance = %+.2w
  FormatSpecUnderTolerance = %+.2w
  Inverted = false
  LineAngle = 0
  LockPosition = false
  MeasureType = 1
  OverTolerance = 0
  References2D = -> [View004]
  Rotation = 0
  ScaleType = 0
  TheoreticalExact = false
  Type = 1
  UnderTolerance = 0
  X = 7.74327
  Y = 19.3764
FEATURE [TechDraw::DrawViewDimension] Dimension026
  AngleOverride = false
  Arbitrary = false
  ArbitraryTolerances = false
  EqualTolerance = true
  ExtensionAngle = 0
  FormatSpec = %.2w
  FormatSpecOverTolerance = %+.2w
  FormatSpecUnderTolerance = %+.2w
  Inverted = false
  LineAngle = 0
  LockPosition = false
  MeasureType = 1
  OverTolerance = 0
  References2D = -> [View004]
  Rotation = 0
  ScaleType = 0
  TheoreticalExact = false
  Type = 2
  UnderTolerance = 0
  X = -11.2372
  Y = 2.12228
FEATURE [TechDraw::DrawViewDimension] Dimension027
  AngleOverride = false
  Arbitrary = false
  ArbitraryTolerances = false
  EqualTolerance = true
  ExtensionAngle = 0
  FormatSpec = R%.2w
  FormatSpecOverTolerance = %+.2w
  FormatSpecUnderTolerance = %+.2w
  Inverted = false
  LineAngle = 0
  LockPosition = false
  MeasureType = 1
  OverTolerance = 0
  References2D = -> [View004]
  Rotation = 0
  ScaleType = 0
  TheoreticalExact = false
  Type = 4
  UnderTolerance = 0
  X = 17.2807
  Y = 19.4526
FEATURE [TechDraw::DrawViewAnnotation] Annotation008
  Font = osifont
  LineSpace = 80
  LockPosition = true
  MaxWidth = -1
  Rotation = 0
  ScaleType = 0
  Text = Sección C - C'
  TextSize = 5
  TextStyle = 0
  X = 112.674
  Y = 142.382
FEATURE [TechDraw::DrawViewAnnotation] Annotation009
  Font = osifont
  LineSpace = 80
  LockPosition = true
  MaxWidth = -1
  Rotation = 0
  ScaleType = 0
  Text = Sección D - D'
  TextSize = 5
  TextStyle = 0
  X = 62.6285
  Y = 141.976
FEATURE [TechDraw::DrawPage] Page  label="Lengüeta"
  KeepUpdated = true
  NextBalloonIndex = 1
  ProjectionType = 0
  Template = -> Template
  Views = -> [ProjGroup,Dimension,Dimension001,View,Dimension003,Dimension004,Dimension005,Dimension006,Dimension007,SectionView,Dimension009,Dimension010,Dimension011,Dimension012,Dimension013,Dimension014,SectionView001,View001,View002,Dimension015,Dimension016,Dimension017,Dimension018,Dimension019,Dimension020,Annotation,Annotation001,Annotation002,Annotation003,Dimension021,LeaderLine,LeaderLine001,+16 more]
note: 4 file-system paths scrubbed to <path> (originals preserved in the JSON sidecar)
